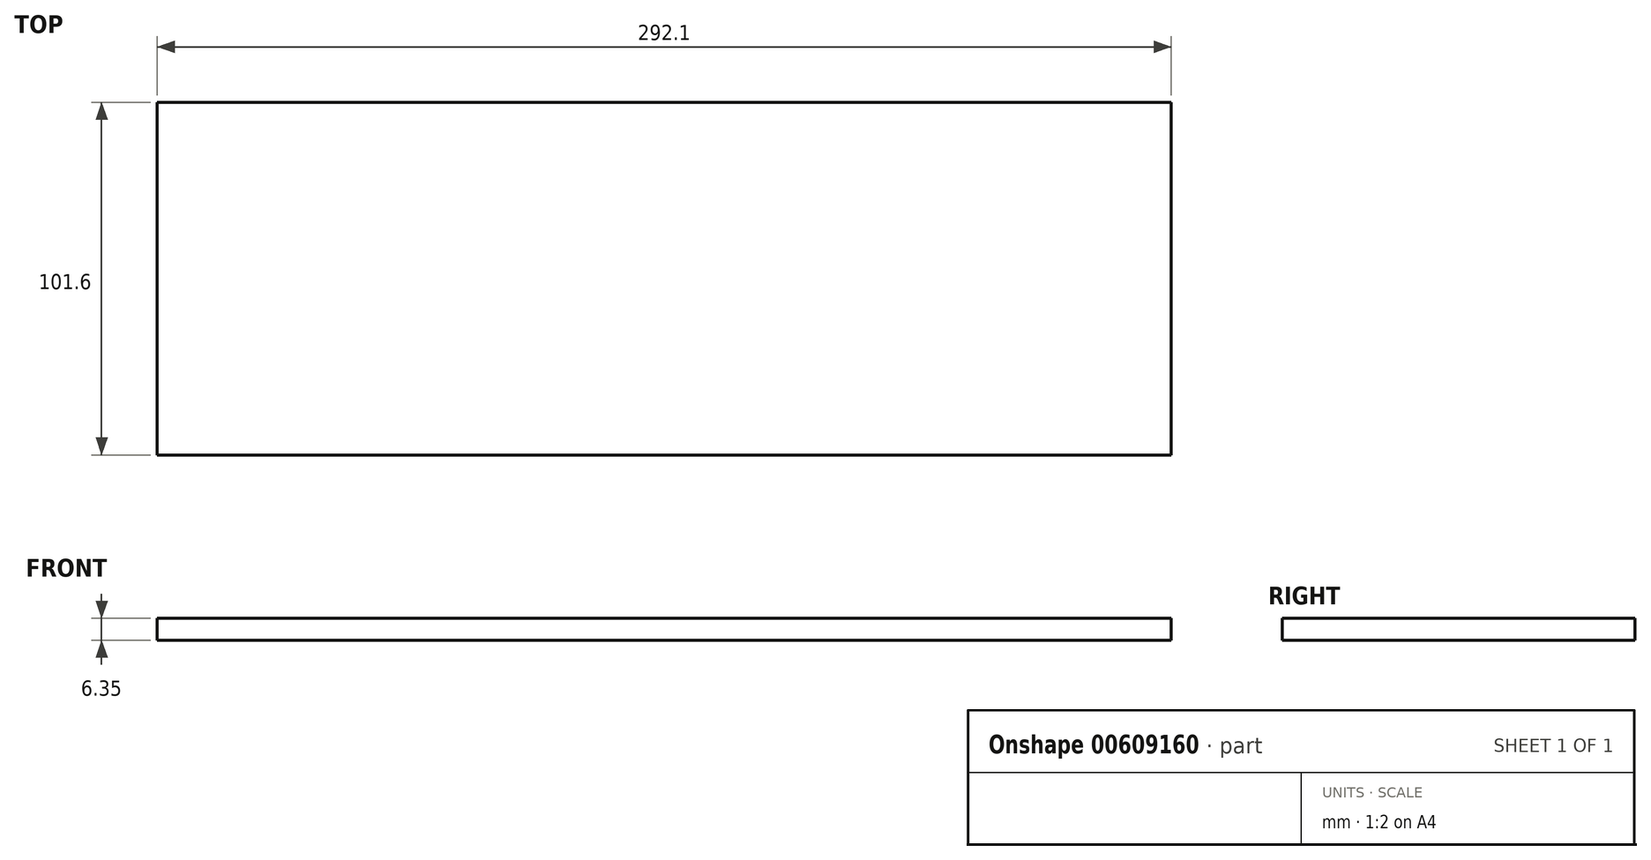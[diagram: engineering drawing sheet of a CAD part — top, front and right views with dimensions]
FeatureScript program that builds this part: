
annotation { "Feature Type Name" : "Feature", "Feature Type Description" : "" }
export const myFeature = defineFeature(function(context is Context, id is Id, definition is map)
    precondition{}
    {
        {
            var Q0;
            Q0=qCreatedBy(makeId("Top.planeOp"),FACE);
            var sketch = newSketch(context, id + "F0", { "sketchPlane" : qUnion([Q0])});
            skLineSegment(sketch, "E0.bottom", {"start": v(0, 0) * mm, "end": v(292.1, 0) * mm});
            skLineSegment(sketch, "E0.top", {"start": v(0, 101.6) * mm, "end": v(292.1, 101.6) * mm});
            skLineSegment(sketch, "E0.left", {"start": v(0, 0) * mm, "end": v(0, 101.6) * mm});
            skLineSegment(sketch, "E0.right", {"start": v(292.1, 0) * mm, "end": v(292.1, 101.6) * mm});
            skSolve(sketch);
        }
        {
            var Q0;
            Q0=makeQuery(id+"F0.imprint","IMPRINT",FACE,{"disambiguationData":[TD([[makeQuery(id+"F0.imprint","IMPRINT",EDGE,{"derivedFrom":sQuery(id+"F0.wireOp",EDGE,"E0.bottom")}),1.0]])]});
            extrude(context, id + "F1", {"entities" : qUnion([Q0]), "depth" : 6.35 * mm, "offsetDistance" : 25.4 * mm});
        }
    });
